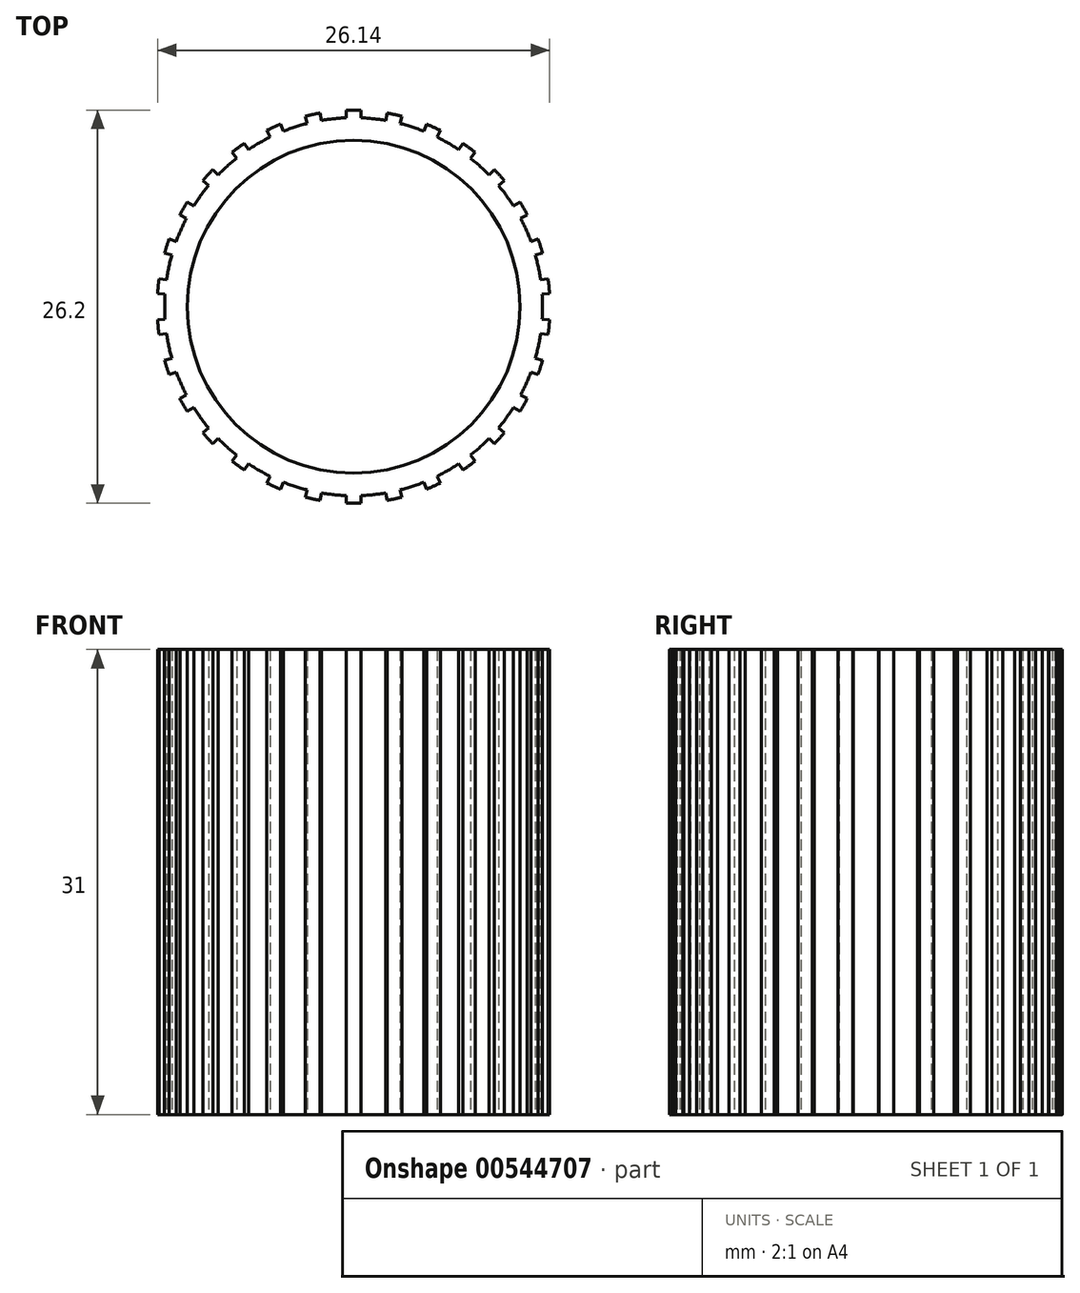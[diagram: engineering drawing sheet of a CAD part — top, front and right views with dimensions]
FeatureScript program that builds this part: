
annotation { "Feature Type Name" : "Feature", "Feature Type Description" : "" }
export const myFeature = defineFeature(function(context is Context, id is Id, definition is map)
    precondition{}
    {
        {
            var Q0;
            Q0=qCreatedBy(makeId("Top.planeOp"),FACE);
            var sketch = newSketch(context, id + "F0", { "sketchPlane" : qUnion([Q0])});
            skCircle(sketch, "E0", {"center": v(0, 0) * mm, "radius": 11.1 * mm});
            skArc(sketch, "E1", {"start": v(0.48, -12.6) * mm, "mid": v(1.32, -12.53) * mm, "end": v(2.15, -12.42) * mm});
            skCircle(sketch, "E2", {"center": v(0, 0) * mm, "radius": 12.5 * mm});
            skArc(sketch, "E3.0", {"start": v(-0.5, -13.1) * mm, "mid": v(0, -13.1) * mm, "end": v(0.5, -13.1) * mm});
            skLineSegment(sketch, "E4", {"start": v(-0.5, -13.1) * mm, "end": v(1.77, -13.18) * mm, "construction": true});
            skLineSegment(sketch, "E5", {"start": v(-0.5, -13.1) * mm, "end": v(-0.48, -12.6) * mm});
            skLineSegment(sketch, "E6.MirrorCS", {"start": v(0.5, -13.1) * mm, "end": v(0.48, -12.6) * mm});
            skLineSegment(sketch, "E7.1.0", {"start": v(2.23, -12.9) * mm, "end": v(2.15, -12.42) * mm});
            skArc(sketch, "E7.1.1", {"start": v(2.23, -12.9) * mm, "mid": v(2.72, -12.81) * mm, "end": v(3.21, -12.7) * mm});
            skLineSegment(sketch, "E7.1.2", {"start": v(3.21, -12.7) * mm, "end": v(3.09, -12.22) * mm});
            skLineSegment(sketch, "E7.2.0", {"start": v(4.87, -12.16) * mm, "end": v(4.68, -11.7) * mm});
            skArc(sketch, "E7.2.1", {"start": v(4.87, -12.16) * mm, "mid": v(5.33, -11.97) * mm, "end": v(5.78, -11.76) * mm});
            skLineSegment(sketch, "E7.2.2", {"start": v(5.78, -11.76) * mm, "end": v(5.56, -11.3) * mm});
            skLineSegment(sketch, "E7.3.0", {"start": v(7.29, -10.88) * mm, "end": v(7.01, -10.47) * mm});
            skArc(sketch, "E7.3.1", {"start": v(7.29, -10.88) * mm, "mid": v(7.7, -10.6) * mm, "end": v(8.1, -10.3) * mm});
            skLineSegment(sketch, "E7.3.2", {"start": v(8.1, -10.3) * mm, "end": v(7.79, -9.9) * mm});
            skLineSegment(sketch, "E7.4.0", {"start": v(9.4, -9.13) * mm, "end": v(9.04, -8.78) * mm});
            skArc(sketch, "E7.4.1", {"start": v(9.4, -9.13) * mm, "mid": v(9.74, -8.77) * mm, "end": v(10.06, -8.39) * mm});
            skLineSegment(sketch, "E7.4.2", {"start": v(10.06, -8.39) * mm, "end": v(9.68, -8.07) * mm});
            skLineSegment(sketch, "E7.5.0", {"start": v(11.09, -6.98) * mm, "end": v(10.66, -6.71) * mm});
            skArc(sketch, "E7.5.1", {"start": v(11.09, -6.98) * mm, "mid": v(11.34, -6.55) * mm, "end": v(11.59, -6.11) * mm});
            skLineSegment(sketch, "E7.5.2", {"start": v(11.59, -6.11) * mm, "end": v(11.14, -5.88) * mm});
            skLineSegment(sketch, "E7.6.0", {"start": v(12.3, -4.52) * mm, "end": v(11.83, -4.35) * mm});
            skArc(sketch, "E7.6.1", {"start": v(12.3, -4.52) * mm, "mid": v(12.46, -4.05) * mm, "end": v(12.6, -3.57) * mm});
            skLineSegment(sketch, "E7.6.2", {"start": v(12.6, -3.57) * mm, "end": v(12.12, -3.43) * mm});
            skLineSegment(sketch, "E7.7.0", {"start": v(12.97, -1.87) * mm, "end": v(12.47, -1.8) * mm});
            skArc(sketch, "E7.7.1", {"start": v(12.97, -1.87) * mm, "mid": v(13.03, -1.37) * mm, "end": v(13.07, -0.87) * mm});
            skLineSegment(sketch, "E7.7.2", {"start": v(13.07, -0.87) * mm, "end": v(12.57, -0.84) * mm});
            skLineSegment(sketch, "E7.8.0", {"start": v(13.07, 0.87) * mm, "end": v(12.57, 0.84) * mm});
            skArc(sketch, "E7.8.1", {"start": v(13.07, 0.87) * mm, "mid": v(13.03, 1.37) * mm, "end": v(12.97, 1.87) * mm});
            skLineSegment(sketch, "E7.8.2", {"start": v(12.97, 1.87) * mm, "end": v(12.47, 1.8) * mm});
            skLineSegment(sketch, "E7.9.0", {"start": v(12.6, 3.57) * mm, "end": v(12.12, 3.43) * mm});
            skArc(sketch, "E7.9.1", {"start": v(12.6, 3.57) * mm, "mid": v(12.46, 4.05) * mm, "end": v(12.3, 4.52) * mm});
            skLineSegment(sketch, "E7.9.2", {"start": v(12.3, 4.52) * mm, "end": v(11.83, 4.35) * mm});
            skLineSegment(sketch, "E7.10.0", {"start": v(11.59, 6.11) * mm, "end": v(11.14, 5.88) * mm});
            skArc(sketch, "E7.10.1", {"start": v(11.59, 6.11) * mm, "mid": v(11.34, 6.55) * mm, "end": v(11.09, 6.98) * mm});
            skLineSegment(sketch, "E7.10.2", {"start": v(11.09, 6.98) * mm, "end": v(10.66, 6.71) * mm});
            skLineSegment(sketch, "E7.11.0", {"start": v(10.06, 8.39) * mm, "end": v(9.68, 8.07) * mm});
            skArc(sketch, "E7.11.1", {"start": v(10.06, 8.39) * mm, "mid": v(9.74, 8.77) * mm, "end": v(9.4, 9.13) * mm});
            skLineSegment(sketch, "E7.11.2", {"start": v(9.4, 9.13) * mm, "end": v(9.04, 8.78) * mm});
            skLineSegment(sketch, "E7.12.0", {"start": v(8.1, 10.3) * mm, "end": v(7.79, 9.9) * mm});
            skArc(sketch, "E7.12.1", {"start": v(8.1, 10.3) * mm, "mid": v(7.7, 10.6) * mm, "end": v(7.29, 10.88) * mm});
            skLineSegment(sketch, "E7.12.2", {"start": v(7.29, 10.88) * mm, "end": v(7.01, 10.47) * mm});
            skLineSegment(sketch, "E7.13.0", {"start": v(5.78, 11.76) * mm, "end": v(5.56, 11.3) * mm});
            skArc(sketch, "E7.13.1", {"start": v(5.78, 11.76) * mm, "mid": v(5.33, 11.97) * mm, "end": v(4.87, 12.16) * mm});
            skLineSegment(sketch, "E7.13.2", {"start": v(4.87, 12.16) * mm, "end": v(4.68, 11.7) * mm});
            skLineSegment(sketch, "E7.14.0", {"start": v(3.21, 12.7) * mm, "end": v(3.09, 12.22) * mm});
            skArc(sketch, "E7.14.1", {"start": v(3.21, 12.7) * mm, "mid": v(2.72, 12.81) * mm, "end": v(2.23, 12.9) * mm});
            skLineSegment(sketch, "E7.14.2", {"start": v(2.23, 12.9) * mm, "end": v(2.15, 12.42) * mm});
            skLineSegment(sketch, "E7.15.0", {"start": v(0.5, 13.1) * mm, "end": v(0.48, 12.6) * mm});
            skArc(sketch, "E7.15.1", {"start": v(0.5, 13.1) * mm, "mid": v(0, 13.1) * mm, "end": v(-0.5, 13.1) * mm});
            skLineSegment(sketch, "E7.15.2", {"start": v(-0.5, 13.1) * mm, "end": v(-0.48, 12.6) * mm});
            skLineSegment(sketch, "E7.16.0", {"start": v(-2.23, 12.9) * mm, "end": v(-2.15, 12.42) * mm});
            skArc(sketch, "E7.16.1", {"start": v(-2.23, 12.9) * mm, "mid": v(-2.72, 12.81) * mm, "end": v(-3.21, 12.7) * mm});
            skLineSegment(sketch, "E7.16.2", {"start": v(-3.21, 12.7) * mm, "end": v(-3.09, 12.22) * mm});
            skLineSegment(sketch, "E7.17.0", {"start": v(-4.87, 12.16) * mm, "end": v(-4.68, 11.7) * mm});
            skArc(sketch, "E7.17.1", {"start": v(-4.87, 12.16) * mm, "mid": v(-5.33, 11.97) * mm, "end": v(-5.78, 11.76) * mm});
            skLineSegment(sketch, "E7.17.2", {"start": v(-5.78, 11.76) * mm, "end": v(-5.56, 11.3) * mm});
            skLineSegment(sketch, "E7.18.0", {"start": v(-7.29, 10.88) * mm, "end": v(-7.01, 10.47) * mm});
            skArc(sketch, "E7.18.1", {"start": v(-7.29, 10.88) * mm, "mid": v(-7.7, 10.6) * mm, "end": v(-8.1, 10.3) * mm});
            skLineSegment(sketch, "E7.18.2", {"start": v(-8.1, 10.3) * mm, "end": v(-7.79, 9.9) * mm});
            skLineSegment(sketch, "E7.19.0", {"start": v(-9.4, 9.13) * mm, "end": v(-9.04, 8.78) * mm});
            skArc(sketch, "E7.19.1", {"start": v(-9.4, 9.13) * mm, "mid": v(-9.74, 8.77) * mm, "end": v(-10.06, 8.39) * mm});
            skLineSegment(sketch, "E7.19.2", {"start": v(-10.06, 8.39) * mm, "end": v(-9.68, 8.07) * mm});
            skArc(sketch, "E8.trimOffspring", {"start": v(-2.15, -12.42) * mm, "mid": v(-1.32, -12.53) * mm, "end": v(-0.48, -12.6) * mm});
            skArc(sketch, "E9.trimOffspring", {"start": v(-7.79, 9.9) * mm, "mid": v(-8.43, 9.36) * mm, "end": v(-9.04, 8.78) * mm});
            skArc(sketch, "E10.trimOffspring", {"start": v(-5.56, 11.3) * mm, "mid": v(-6.3, 10.91) * mm, "end": v(-7.01, 10.47) * mm});
            skArc(sketch, "E11.trimOffspring", {"start": v(3.09, -12.22) * mm, "mid": v(3.9, -11.98) * mm, "end": v(4.68, -11.7) * mm});
            skArc(sketch, "E12.trimOffspring", {"start": v(5.56, -11.3) * mm, "mid": v(6.3, -10.91) * mm, "end": v(7.01, -10.47) * mm});
            skArc(sketch, "E13.trimOffspring", {"start": v(-3.09, 12.22) * mm, "mid": v(-3.9, 11.98) * mm, "end": v(-4.68, 11.7) * mm});
            skArc(sketch, "E14.trimOffspring", {"start": v(-0.48, 12.6) * mm, "mid": v(-1.32, 12.53) * mm, "end": v(-2.15, 12.42) * mm});
            skArc(sketch, "E15.trimOffspring", {"start": v(2.15, 12.42) * mm, "mid": v(1.32, 12.53) * mm, "end": v(0.48, 12.6) * mm});
            skArc(sketch, "E16.trimOffspring", {"start": v(4.68, 11.7) * mm, "mid": v(3.9, 11.98) * mm, "end": v(3.09, 12.22) * mm});
            skArc(sketch, "E17.trimOffspring", {"start": v(7.01, 10.47) * mm, "mid": v(6.3, 10.91) * mm, "end": v(5.56, 11.3) * mm});
            skArc(sketch, "E18.trimOffspring", {"start": v(9.04, 8.78) * mm, "mid": v(8.43, 9.36) * mm, "end": v(7.79, 9.9) * mm});
            skArc(sketch, "E19.trimOffspring", {"start": v(10.66, 6.71) * mm, "mid": v(10.2, 7.4) * mm, "end": v(9.68, 8.07) * mm});
            skArc(sketch, "E20.trimOffspring", {"start": v(11.83, 4.35) * mm, "mid": v(11.51, 5.12) * mm, "end": v(11.14, 5.88) * mm});
            skArc(sketch, "E21.trimOffspring", {"start": v(12.47, 1.8) * mm, "mid": v(12.32, 2.62) * mm, "end": v(12.12, 3.43) * mm});
            skArc(sketch, "E22.trimOffspring", {"start": v(12.57, -0.84) * mm, "mid": v(12.6, 0) * mm, "end": v(12.57, 0.84) * mm});
            skArc(sketch, "E23.trimOffspring", {"start": v(12.12, -3.43) * mm, "mid": v(12.32, -2.62) * mm, "end": v(12.47, -1.8) * mm});
            skArc(sketch, "E24.trimOffspring", {"start": v(11.14, -5.88) * mm, "mid": v(11.51, -5.12) * mm, "end": v(11.83, -4.35) * mm});
            skArc(sketch, "E25.trimOffspring", {"start": v(9.68, -8.07) * mm, "mid": v(10.2, -7.4) * mm, "end": v(10.66, -6.71) * mm});
            skArc(sketch, "E26.trimOffspring", {"start": v(7.79, -9.9) * mm, "mid": v(8.43, -9.36) * mm, "end": v(9.04, -8.78) * mm});
            skLineSegment(sketch, "E27.1.20.0", {"start": v(-11.09, 6.98) * mm, "end": v(-10.66, 6.71) * mm});
            skArc(sketch, "E27.3.20.0", {"start": v(-11.09, 6.98) * mm, "mid": v(-11.34, 6.55) * mm, "end": v(-11.59, 6.11) * mm});
            skLineSegment(sketch, "E27.7.20.0", {"start": v(-11.59, 6.11) * mm, "end": v(-11.14, 5.88) * mm});
            skLineSegment(sketch, "E28.1.21.0", {"start": v(-12.3, 4.52) * mm, "end": v(-11.83, 4.35) * mm});
            skArc(sketch, "E28.3.21.0", {"start": v(-12.3, 4.52) * mm, "mid": v(-12.46, 4.05) * mm, "end": v(-12.6, 3.57) * mm});
            skLineSegment(sketch, "E28.7.21.0", {"start": v(-12.6, 3.57) * mm, "end": v(-12.12, 3.43) * mm});
            skLineSegment(sketch, "E29.1.22.0", {"start": v(-12.97, 1.87) * mm, "end": v(-12.47, 1.8) * mm});
            skArc(sketch, "E29.3.22.0", {"start": v(-12.97, 1.87) * mm, "mid": v(-13.03, 1.37) * mm, "end": v(-13.07, 0.87) * mm});
            skLineSegment(sketch, "E29.7.22.0", {"start": v(-13.07, 0.87) * mm, "end": v(-12.57, 0.84) * mm});
            skLineSegment(sketch, "E30.1.23.0", {"start": v(-13.07, -0.87) * mm, "end": v(-12.57, -0.84) * mm});
            skArc(sketch, "E30.3.23.0", {"start": v(-13.07, -0.87) * mm, "mid": v(-13.03, -1.37) * mm, "end": v(-12.97, -1.87) * mm});
            skLineSegment(sketch, "E30.7.23.0", {"start": v(-12.97, -1.87) * mm, "end": v(-12.47, -1.8) * mm});
            skLineSegment(sketch, "E31.1.24.0", {"start": v(-12.6, -3.57) * mm, "end": v(-12.12, -3.43) * mm});
            skArc(sketch, "E31.3.24.0", {"start": v(-12.6, -3.57) * mm, "mid": v(-12.46, -4.05) * mm, "end": v(-12.3, -4.52) * mm});
            skLineSegment(sketch, "E31.7.24.0", {"start": v(-12.3, -4.52) * mm, "end": v(-11.83, -4.35) * mm});
            skLineSegment(sketch, "E32.1.25.0", {"start": v(-11.59, -6.11) * mm, "end": v(-11.14, -5.88) * mm});
            skArc(sketch, "E32.3.25.0", {"start": v(-11.59, -6.11) * mm, "mid": v(-11.34, -6.55) * mm, "end": v(-11.09, -6.98) * mm});
            skLineSegment(sketch, "E32.7.25.0", {"start": v(-11.09, -6.98) * mm, "end": v(-10.66, -6.71) * mm});
            skLineSegment(sketch, "E33.1.26.0", {"start": v(-10.06, -8.39) * mm, "end": v(-9.68, -8.07) * mm});
            skArc(sketch, "E33.3.26.0", {"start": v(-10.06, -8.39) * mm, "mid": v(-9.74, -8.77) * mm, "end": v(-9.4, -9.13) * mm});
            skLineSegment(sketch, "E33.7.26.0", {"start": v(-9.4, -9.13) * mm, "end": v(-9.04, -8.78) * mm});
            skLineSegment(sketch, "E34.1.27.0", {"start": v(-8.1, -10.3) * mm, "end": v(-7.79, -9.9) * mm});
            skArc(sketch, "E34.3.27.0", {"start": v(-8.1, -10.3) * mm, "mid": v(-7.7, -10.6) * mm, "end": v(-7.29, -10.88) * mm});
            skLineSegment(sketch, "E34.7.27.0", {"start": v(-7.29, -10.88) * mm, "end": v(-7.01, -10.47) * mm});
            skArc(sketch, "E35.trimOffspring", {"start": v(-9.04, -8.78) * mm, "mid": v(-8.43, -9.36) * mm, "end": v(-7.79, -9.9) * mm});
            skArc(sketch, "E36.trimOffspring", {"start": v(-10.66, -6.71) * mm, "mid": v(-10.2, -7.4) * mm, "end": v(-9.68, -8.07) * mm});
            skArc(sketch, "E37.trimOffspring", {"start": v(-11.83, -4.35) * mm, "mid": v(-11.51, -5.12) * mm, "end": v(-11.14, -5.88) * mm});
            skArc(sketch, "E38.trimOffspring", {"start": v(-12.47, -1.8) * mm, "mid": v(-12.32, -2.62) * mm, "end": v(-12.12, -3.43) * mm});
            skArc(sketch, "E39.trimOffspring", {"start": v(-12.57, 0.84) * mm, "mid": v(-12.6, 0) * mm, "end": v(-12.57, -0.84) * mm});
            skArc(sketch, "E40.trimOffspring", {"start": v(-12.12, 3.43) * mm, "mid": v(-12.32, 2.62) * mm, "end": v(-12.47, 1.8) * mm});
            skArc(sketch, "E41.trimOffspring", {"start": v(-9.68, 8.07) * mm, "mid": v(-10.2, 7.4) * mm, "end": v(-10.66, 6.71) * mm});
            skArc(sketch, "E42.trimOffspring", {"start": v(-11.14, 5.88) * mm, "mid": v(-11.51, 5.12) * mm, "end": v(-11.83, 4.35) * mm});
            skLineSegment(sketch, "E43.1.28.0", {"start": v(-5.78, -11.76) * mm, "end": v(-5.56, -11.3) * mm});
            skArc(sketch, "E43.3.28.0", {"start": v(-5.78, -11.76) * mm, "mid": v(-5.33, -11.97) * mm, "end": v(-4.87, -12.16) * mm});
            skLineSegment(sketch, "E43.7.28.0", {"start": v(-4.87, -12.16) * mm, "end": v(-4.68, -11.7) * mm});
            skLineSegment(sketch, "E43.1.29.0", {"start": v(-3.21, -12.7) * mm, "end": v(-3.09, -12.22) * mm});
            skArc(sketch, "E43.3.29.0", {"start": v(-3.21, -12.7) * mm, "mid": v(-2.72, -12.81) * mm, "end": v(-2.23, -12.9) * mm});
            skLineSegment(sketch, "E43.7.29.0", {"start": v(-2.23, -12.9) * mm, "end": v(-2.15, -12.42) * mm});
            skArc(sketch, "E44.trimOffspring", {"start": v(-4.68, -11.7) * mm, "mid": v(-3.9, -11.98) * mm, "end": v(-3.09, -12.22) * mm});
            skArc(sketch, "E45.trimOffspring", {"start": v(-7.01, -10.47) * mm, "mid": v(-6.3, -10.91) * mm, "end": v(-5.56, -11.3) * mm});
            skSolve(sketch);
        }
        {
            var Q0;
            Q0 = qSketchRegion(id + "F0", true);
            extrude(context, id + "F1", {"entities" : qUnion([Q0]), "endBound" : BoundingType.SYMMETRIC, "depth" : 31 * mm, "offsetDistance" : 25 * mm});
        }
        {
            var Q0;
            Q0=makeQuery(id+"F0.imprint","IMPRINT",FACE,{"disambiguationData":[TD([[makeQuery(id+"F0.imprint","IMPRINT",EDGE,{"derivedFrom":sQuery(id+"F0.wireOp",EDGE,"E0")}),-1.0]])]});
            extrude(context, id + "F2", {"entities" : qUnion([Q0]), "operationType" : NewBodyOperationType.ADD, "endBound" : BoundingType.SYMMETRIC, "depth" : 31 * mm, "offsetDistance" : 25 * mm});
        }
    });
